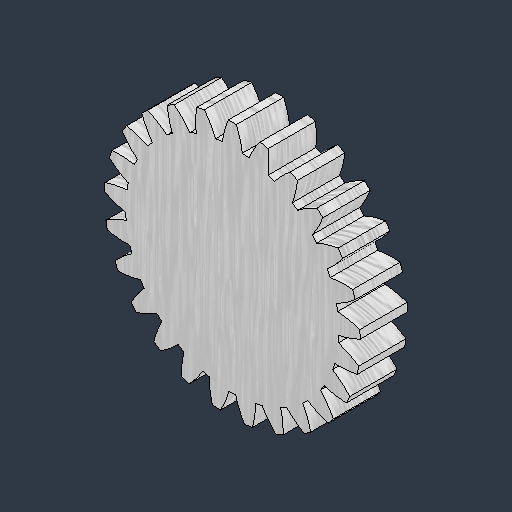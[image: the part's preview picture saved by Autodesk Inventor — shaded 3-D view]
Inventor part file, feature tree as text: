
AUTODESK INVENTOR PART (.ipt)
format: ipt  version: 2024.3 (Build 283343000, 343)  size: 302,080 bytes
history: native  units: mm (DEFAULTED — no unit token found)
features: plane x3, other x3, extrude x1, sketch x1
ambient origin geometry x8: Origin, YZ Plane, XZ Plane, XY Plane, X Axis, Y Axis, Z Axis, Center Point
bodies: Solid1 (feature_tree)
feature tree (8):
  extrude  "Extrusion1"  Depth=12.7mm TaperAngle=0.0deg
  plane  "Work Plane1"
  plane  "Work Plane2"
  plane  "Work Plane3"
  other  "Spur Gear"
  sketch  "Sketch1"  dims[d0=68.58mm d1=12.7mm d2=0.0mm d3=63.5mm d4=76.2mm d5=0.0mm d6=0.0mm d7=1.256637mm d9=0.0mm d14=0.0mm d15=158.75mm d16=0.0mm d17=0.0mm d18=0.0mm d19=158.75mm]
  other  "Srf1"
  other  "Pitch Diameter"
